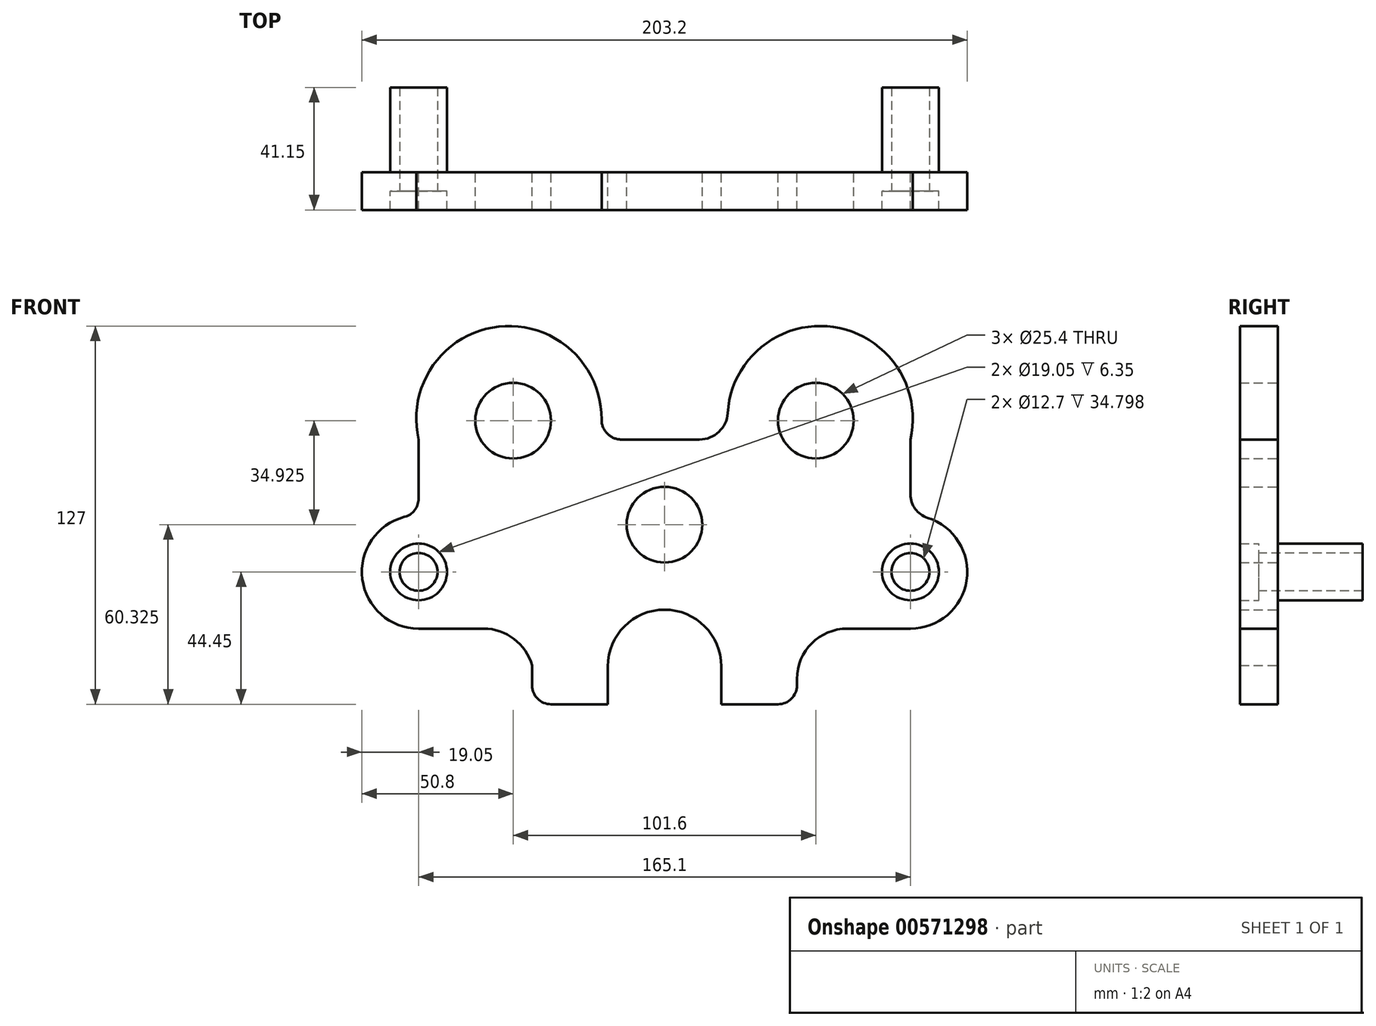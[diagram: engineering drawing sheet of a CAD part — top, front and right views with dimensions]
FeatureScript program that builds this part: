
annotation { "Feature Type Name" : "Feature", "Feature Type Description" : "" }
export const myFeature = defineFeature(function(context is Context, id is Id, definition is map)
    precondition{}
    {
        {
            var Q0;
            Q0=qCreatedBy(makeId("Front.planeOp"),FACE);
            var sketch = newSketch(context, id + "F0", { "sketchPlane" : qUnion([Q0])});
            skLineSegment(sketch, "E0", {"start": v(0, 125.05) * mm, "end": v(0, -126.03) * mm, "construction": true});
            skLineSegment(sketch, "E1", {"start": v(0, 63.5) * mm, "end": v(11.75, 63.5) * mm});
            skArc(sketch, "E2", {"start": v(82.55, 63.5) * mm, "mid": v(56.7, 101.28) * mm, "end": v(21.2, 72.4) * mm});
            skLineSegment(sketch, "E3", {"start": v(82.55, 63.5) * mm, "end": v(82.55, 45.06) * mm});
            skArc(sketch, "E4", {"start": v(82.55, 0) * mm, "mid": v(101.38, 16.14) * mm, "end": v(88.3, 37.21) * mm});
            skLineSegment(sketch, "E5", {"start": v(38.1, -25.4) * mm, "end": v(19.05, -25.4) * mm});
            skLineSegment(sketch, "E6.MirrorCS", {"start": v(0, 63.5) * mm, "end": v(-14.47, 63.5) * mm});
            skArc(sketch, "E7.MirrorCS", {"start": v(-82.55, 63.5) * mm, "mid": v(-55.63, 101.41) * mm, "end": v(-21.14, 70.23) * mm});
            skLineSegment(sketch, "E8.MirrorCS", {"start": v(-82.55, 63.5) * mm, "end": v(-82.55, 43.64) * mm});
            skArc(sketch, "E9.MirrorCS", {"start": v(-82.55, 0) * mm, "mid": v(-101.45, 16.65) * mm, "end": v(-87.31, 37.5) * mm});
            skLineSegment(sketch, "E10.MirrorCS", {"start": v(-38.1, -25.4) * mm, "end": v(-19.05, -25.4) * mm});
            skCircle(sketch, "E11", {"center": v(0, 34.93) * mm, "radius": 12.7 * mm});
            skCircle(sketch, "E12", {"center": v(82.55, 19.05) * mm, "radius": 6.35 * mm});
            skCircle(sketch, "E13", {"center": v(-82.55, 19.05) * mm, "radius": 6.35 * mm});
            skPoint(sketch, "E14.visualSharp", {"position": v(82.55, 38.1) * mm});
            skArc(sketch, "E14.filletArc", {"start": v(82.55, 45.06) * mm, "mid": v(84.14, 40.2) * mm, "end": v(88.3, 37.21) * mm});
            skPoint(sketch, "E15.visualSharp", {"position": v(21.94, 63.5) * mm});
            skArc(sketch, "E15.filletArc", {"start": v(11.75, 63.5) * mm, "mid": v(18.24, 66.07) * mm, "end": v(21.2, 72.4) * mm});
            skPoint(sketch, "E16.visualSharp", {"position": v(-21.94, 63.5) * mm});
            skArc(sketch, "E16.filletArc", {"start": v(-21.14, 70.23) * mm, "mid": v(-19.21, 65.47) * mm, "end": v(-14.47, 63.5) * mm});
            skPoint(sketch, "E17.visualSharp", {"position": v(-82.55, 38.1) * mm});
            skArc(sketch, "E17.filletArc", {"start": v(-87.31, 37.5) * mm, "mid": v(-83.88, 39.75) * mm, "end": v(-82.55, 43.64) * mm});
            skCircle(sketch, "E18", {"center": v(-50.8, 69.85) * mm, "radius": 12.7 * mm});
            skCircle(sketch, "E19", {"center": v(50.8, 69.85) * mm, "radius": 12.7 * mm});
            skLineSegment(sketch, "E20", {"start": v(-19.05, -25.4) * mm, "end": v(-19.05, -12.7) * mm});
            skLineSegment(sketch, "E21", {"start": v(0, 6.35) * mm, "end": v(0, 6.35) * mm});
            skLineSegment(sketch, "E22", {"start": v(19.05, -12.7) * mm, "end": v(19.05, -25.4) * mm});
            skPoint(sketch, "E23.visualSharp", {"position": v(-19.05, 6.35) * mm});
            skArc(sketch, "E23.filletArc", {"start": v(0, 6.35) * mm, "mid": v(-13.47, 0.77) * mm, "end": v(-19.05, -12.7) * mm});
            skPoint(sketch, "E24.visualSharp", {"position": v(19.05, 6.35) * mm});
            skArc(sketch, "E24.filletArc", {"start": v(19.05, -12.7) * mm, "mid": v(13.47, 0.77) * mm, "end": v(0, 6.35) * mm});
            skLineSegment(sketch, "E25", {"start": v(-82.55, 0) * mm, "end": v(-60.76, 0) * mm});
            skPoint(sketch, "E26.visualSharp", {"position": v(-37.17, 0) * mm});
            skArc(sketch, "E26.filletArc", {"start": v(-44.45, -12.4) * mm, "mid": v(-50.52, -3.45) * mm, "end": v(-60.76, 0) * mm});
            skLineSegment(sketch, "E27", {"start": v(82.55, 0) * mm, "end": v(61.38, 0) * mm});
            skLineSegment(sketch, "E28", {"start": v(44.45, -16.93) * mm, "end": v(44.45, -19.05) * mm});
            skPoint(sketch, "E29.visualSharp", {"position": v(44.45, 0) * mm});
            skArc(sketch, "E29.filletArc", {"start": v(61.38, 0) * mm, "mid": v(49.4, -4.96) * mm, "end": v(44.45, -16.93) * mm});
            skLineSegment(sketch, "E30", {"start": v(-44.45, -12.4) * mm, "end": v(-44.45, -19.05) * mm});
            skPoint(sketch, "E31.visualSharp", {"position": v(44.45, -25.4) * mm});
            skArc(sketch, "E31.filletArc", {"start": v(38.1, -25.4) * mm, "mid": v(42.6, -23.54) * mm, "end": v(44.45, -19.05) * mm});
            skPoint(sketch, "E32.visualSharp", {"position": v(-44.45, -25.4) * mm});
            skArc(sketch, "E32.filletArc", {"start": v(-44.45, -19.05) * mm, "mid": v(-42.6, -23.54) * mm, "end": v(-38.1, -25.4) * mm});
            skCircle(sketch, "E33", {"center": v(-82.55, 19.05) * mm, "radius": 9.53 * mm});
            skCircle(sketch, "E34", {"center": v(82.55, 19.05) * mm, "radius": 9.53 * mm});
            skSolve(sketch);
        }
        {
            var Q0;
            Q0=makeQuery(id+"F0.imprint","IMPRINT",FACE,{"disambiguationData":[TD([[makeQuery(id+"F0.imprint","IMPRINT",EDGE,{"derivedFrom":sQuery(id+"F0.wireOp",EDGE,"E1")}),-1.0]])]});
            extrude(context, id + "F1", {"entities" : qUnion([Q0]), "endBound" : BoundingType.SYMMETRIC, "depth" : 12.7 * mm, "offsetDistance" : 25.4 * mm});
        }
        {
            var Q0;
            Q0=makeQuery(id+"F0.imprint","IMPRINT",FACE,{"disambiguationData":[TD([[makeQuery(id+"F0.imprint","IMPRINT",EDGE,{"derivedFrom":sQuery(id+"F0.wireOp",EDGE,"E12")}),-1.0]])]});
            var Q1;
            Q1=makeQuery(id+"F0.imprint","IMPRINT",FACE,{"disambiguationData":[TD([[makeQuery(id+"F0.imprint","IMPRINT",EDGE,{"derivedFrom":sQuery(id+"F0.wireOp",EDGE,"E13")}),-1.0]])]});
            extrude(context, id + "F2", {"entities" : qUnion([Q0, Q1]), "operationType" : NewBodyOperationType.ADD, "oppositeDirection" : true, "depth" : 34.8 * mm, "offsetDistance" : 25.4 * mm});
        }
    });
